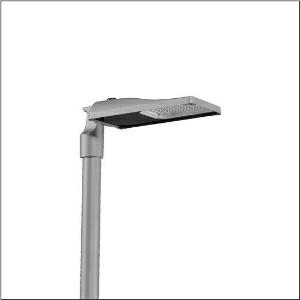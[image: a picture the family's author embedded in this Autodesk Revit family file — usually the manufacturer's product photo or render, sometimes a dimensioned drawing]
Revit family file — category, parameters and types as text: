
# Revit family: streetlight_sl_31_mini___st1_0a_5xh2d31s08ja_14e0
name_source: partatom
category: Lighting Fixtures
units: mm (PartAtom-declared; Revit-internal decimal feet)

## family parameters
Cut with Voids When Loaded = No
Host = Face
Light Source = No
Part Type = Normal
Room Calculation Point = No
Round Connector Dimension = Use Diameter
Shared = No

## types (1)
- --- (1 x LED, 12270 lm, 82.5 W, 3000K)
    Apparent Load = 83 VA
    CIE Flux Codes = 40 73 97 100 100
    Color Rendering = 70
    Color Temperature = 3000K
    Default Elevation = 1800 mm
    Description = Streetlight SL 31 mini D4i, Desk-Remote mast luminaire for post-top, side-entry; light control with lens of PMMA; light distribution: ST1.0a, direct asymmetric distribution, for standard-compliant lighting for roads and squares; LED: luminous flux: 12.270lm, light colour: 730, colour temperature: 3000K; luminous efficacy: 148,7lm/W; control: pre-setting: logarithmic dimming characteristic, flexible luminous flux parameterisation, time-dependent luminous flux control, constant luminous flux control, power reduction, intelligent temperature release in ECG and LED module, overheat protection; luminaire housing, of diecast aluminium, SITECO metallic grey (DB 702S), corrosivity category C5 high according to DIN EN ISO 12944; cover of toughened safety glass, transparent, mast flange of diecast aluminium, SITECO metallic grey (DB 702S), spigot size: 76/60mm, mast flange included unmounted; with cable H07RN-F 2x 1.5mm², cable length: 10,5m, connection cable pre-assembled; mains connection: 220..240V, AC, 50/60Hz; power consumption (at start of service life): 82,5W / (at end of service life): 90,1W / (with reduced operation 50%): 36,8W; protection rating (complete): IP66; insulation class (complete): insulation class II (safety insulation); impact resistance: IK10; certification: CE, ENEC, ENEC+, VDE, UKCA, ZD4i; permissible operating ambient temperature for outdoor applications: -40..+50°C; packaging unit: 1 piece

Light Distribution: ST1.0a
    Height = 76 mm
    Lamp = 1 x LED
    Lamp Light Flux = 12270 lm
    Lamp Power = 82.5 W
    Lamp count = 1
    Length = 547 mm
    Luminous efficacy = 149 lm/W
    Manufacturer = Siteco
    ModVariant = No
    Model = 5XH2D31S08JA
    Number of Poles = 1
    OnlyDefault = Yes
    Power Factor = 1
    Product Name = Streetlight SL 31 mini | ST1.0a
    Product group = mast luminaire | pylon top
    ProductGroupID = 6100
    Protection Class = Protection class II
    Protection Degree = IP 66
    RLX_Detail_Level = 1
    RLX_Emergency_Light_Flux = 0 lm
    RLX_Emergency_Type = 0
    RLX_Emergency_Type_DB = No
    RlxData = <blob elided: 39693 chars, md5=3c17db04>
    Socket = socket
    Standby Power = 0 W
    System Light Flux = 12270 lm
    System Power = 83 W
    Type Comments = factory setting: luminous flux: 100 % | dim-lin: 254 | 870 mA
    Type Image = l_1300330.jpg
    URL = http://relux.com
    VarID = @adj_057715
    Voltage = 0 V
    Weight = 0.00 kg
    Width = 265 mm

## geometry (parser evidence)
native form markers: Blend x4, Sweep x9
no freeform markers — native parametric forms only
